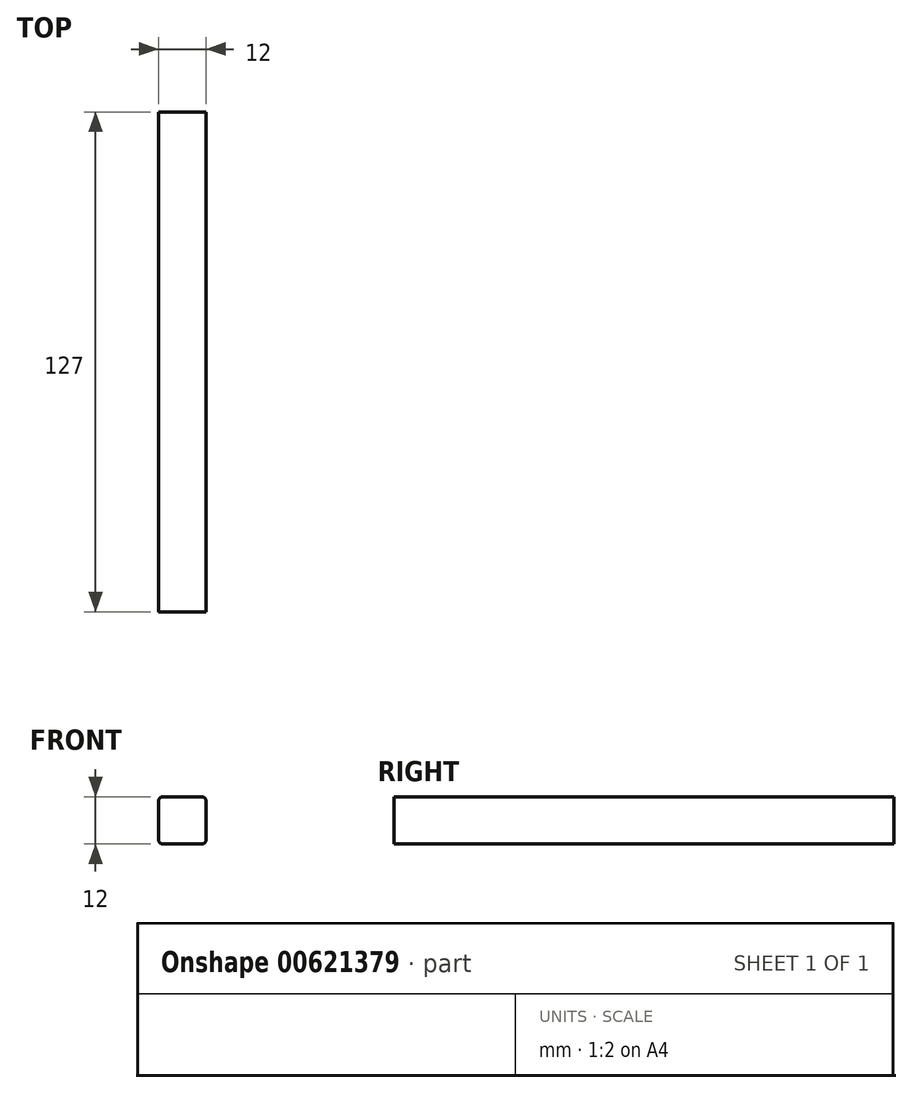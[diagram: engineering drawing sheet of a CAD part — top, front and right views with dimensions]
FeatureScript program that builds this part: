
annotation { "Feature Type Name" : "Feature", "Feature Type Description" : "" }
export const myFeature = defineFeature(function(context is Context, id is Id, definition is map)
    precondition{}
    {
        {
            var Q0;
            Q0=qCreatedBy(makeId("Front.planeOp"),FACE);
            var sketch = newSketch(context, id + "F0", { "sketchPlane" : qUnion([Q0])});
            skLineSegment(sketch, "E0.bottom", {"start": v(6, -6) * mm, "end": v(-6, -6) * mm});
            skLineSegment(sketch, "E0.top", {"start": v(6, 6) * mm, "end": v(-6, 6) * mm});
            skLineSegment(sketch, "E0.left", {"start": v(6, -6) * mm, "end": v(6, 6) * mm});
            skLineSegment(sketch, "E0.right", {"start": v(-6, -6) * mm, "end": v(-6, 6) * mm});
            skPoint(sketch, "E0.middle", {"position": v(0, 0) * mm});
            skSolve(sketch);
        }
        {
            var Q0;
            Q0 = qSketchRegion(id + "F0", true);
            extrude(context, id + "F1", {"entities" : qUnion([Q0]), "depth" : 127 * mm, "offsetDistance" : 25 * mm});
        }
        {
            var Q0;
            Q0=makeQuery(id+"F1.opExtrude","SWEPT_EDGE",EDGE,{"disambiguationData":[OSD([sQuery(id+"F0.wireOp",EDGE,"E0.top"),sQuery(id+"F0.wireOp",EDGE,"E0.left")])]});
            var Q1;
            Q1=makeQuery(id+"F1.opExtrude","SWEPT_EDGE",EDGE,{"disambiguationData":[OSD([sQuery(id+"F0.wireOp",EDGE,"E0.top"),sQuery(id+"F0.wireOp",EDGE,"E0.right")])]});
            var Q2;
            Q2=makeQuery(id+"F1.opExtrude","SWEPT_EDGE",EDGE,{"disambiguationData":[OSD([sQuery(id+"F0.wireOp",EDGE,"E0.bottom"),sQuery(id+"F0.wireOp",EDGE,"E0.left")])]});
            var Q3;
            Q3=makeQuery(id+"F1.opExtrude","SWEPT_EDGE",EDGE,{"disambiguationData":[OSD([sQuery(id+"F0.wireOp",EDGE,"E0.bottom"),sQuery(id+"F0.wireOp",EDGE,"E0.right")])]});
            fillet(context, id + "F2", {"entities" : qUnion([Q0, Q1, Q2, Q3]), "radius" : 1 * mm, "tangentPropagation" : true, "allowEdgeOverflow" : false});
        }
    });
